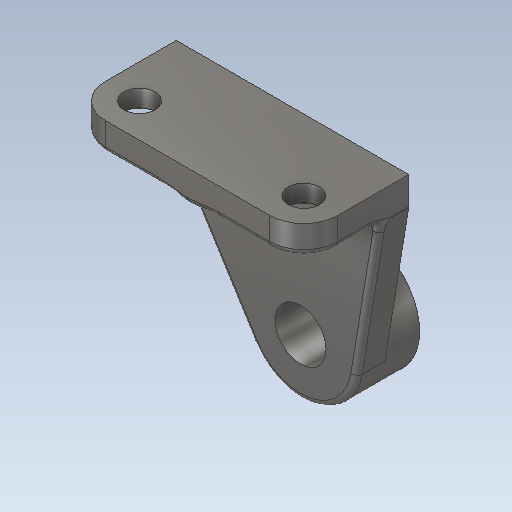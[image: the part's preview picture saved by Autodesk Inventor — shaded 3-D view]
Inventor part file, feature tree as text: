
AUTODESK INVENTOR PART (.ipt)
format: ipt  version: 2020 (Build 240168000, 168)  size: 338,432 bytes
history: native  units: mm
features: extrude x5, sketch x4, fillet x2, plane x1, rib x1
ambient origin geometry x8: Origin, YZ Plane, XZ Plane, XY Plane, X Axis, Y Axis, Z Axis, Center Point
bodies: Solid1 (feature_tree)
feature tree (13):
  extrude  "Extrusion1"  Depth=41.0mm
  sketch  "Sketch2"  dims[d2=18.0mm d3=22.0mm d4=0.0mm]
  extrude  "Extrusion2"  Depth=22.0mm TaperAngle=0.0deg
  extrude  "Extrusion3"  Depth=10.0mm
  plane  "Work Plane1"
  rib  "Rib1"
  sketch  "Sketch6"  dims[d8=10.0mm d9=0.0mm d10=27.0mm d11=0.0mm d12=-41.0mm d17=1.0mm d18=10.0mm d19=0.0mm d20=0.0mm d21=1.0mm d22=1.0mm d23=11.0mm d24=22.0mm d25=22.0mm d26=11.0mm d27=12.0mm d28=12.0mm d29=12.0mm d30=12.0mm d31=27.0mm d32=0.0mm d33=4.0mm d34=0.0mm d35=12.0mm d37=2.0mm d38=48.0mm d40=53.861561mm]
  extrude  "Extrusion4"  Depth=2.0mm TaperAngle=0.0deg
  extrude  "Extrusion5"  [1 undecoded]
  fillet  "Fillet1"  Radius=1.0mm
  fillet  "Fillet3"  Radius=11.0mm
  sketch  "Sketch1"  dims[d0=40.0mm d1=41.0mm]
  sketch  "Sketch5"  dims[d5=82.0mm d7=10.0mm]
note: 1 required parameter value undecoded (feature->parameter linkage not recoverable at this tier; creation-order binding heuristic only, values carry confidence <= 0.55)
